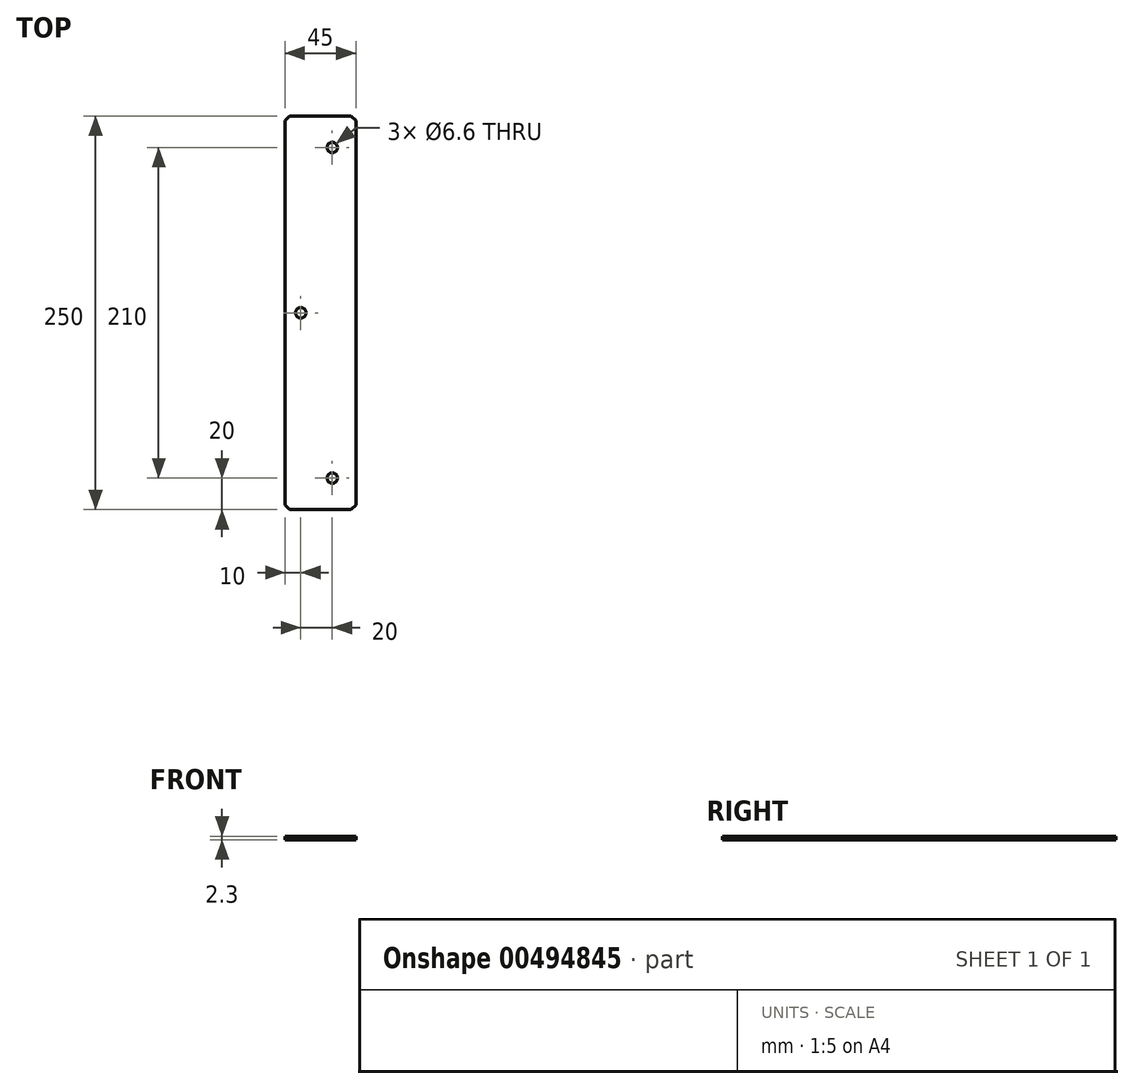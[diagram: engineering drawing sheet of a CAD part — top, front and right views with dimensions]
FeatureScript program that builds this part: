
annotation { "Feature Type Name" : "Feature", "Feature Type Description" : "" }
export const myFeature = defineFeature(function(context is Context, id is Id, definition is map)
    precondition{}
    {
        {
            var Q0;
            Q0=qCreatedBy(makeId("Top.planeOp"),FACE);
            var sketch = newSketch(context, id + "F0", { "sketchPlane" : qUnion([Q0])});
            skLineSegment(sketch, "E0.bottom", {"start": v(0, 0) * mm, "end": v(45, 0) * mm});
            skLineSegment(sketch, "E0.top", {"start": v(0, 250) * mm, "end": v(45, 250) * mm});
            skLineSegment(sketch, "E0.left", {"start": v(0, 0) * mm, "end": v(0, 250) * mm});
            skLineSegment(sketch, "E0.right", {"start": v(45, 0) * mm, "end": v(45, 250) * mm});
            skSolve(sketch);
        }
        {
            var Q0;
            Q0=qSketchRegion(id+"F0",true);
            extrude(context, id + "F1", {"entities" : qUnion([Q0]), "depth" : 2.3 * mm});
        }
        {
            var Q0;
            Q0=makeQuery(id+"F1.opExtrude","CAP_FACE",FACE,{"disambiguationData":[OSD([sQuery(id+"F0.wireOp",EDGE,"E0.bottom"),sQuery(id+"F0.wireOp",EDGE,"E0.top"),sQuery(id+"F0.wireOp",EDGE,"E0.left"),sQuery(id+"F0.wireOp",EDGE,"E0.right")])],"isStart":false});
            var sketch = newSketch(context, id + "F2", { "sketchPlane" : qUnion([Q0])});
            skPoint(sketch, "E1", {"position": v(30, 230) * mm});
            skPoint(sketch, "E2", {"position": v(10, 125) * mm});
            skPoint(sketch, "E3", {"position": v(30, 20) * mm});
            skSolve(sketch);
        }
        {
            var Q0;
            Q0=sQuery(id+"F2.wireOp",VERTEX,"E1");
            var Q1;
            Q1=sQuery(id+"F2.wireOp",VERTEX,"E2");
            var Q2;
            Q2=sQuery(id+"F2.wireOp",VERTEX,"E3");
            var Q3;
            Q3=makeQuery(id+"F1.opExtrude","SWEPT_BODY",BODY,{"disambiguationData":[OSD([sQuery(id+"F0.wireOp",EDGE,"E0.bottom"),sQuery(id+"F0.wireOp",EDGE,"E0.top"),sQuery(id+"F0.wireOp",EDGE,"E0.left"),sQuery(id+"F0.wireOp",EDGE,"E0.right")])]});
            hole(context, id + "F3", {"style" : HoleStyle.SIMPLE, "endStyle" : HoleEndStyle.THROUGH, "standardTappedOrClearance" : lookupTablePath({ "standard" : "ISO", "fit" : "Normal", "size" : "M6", "type" : "Clearance" }), "standardBlindInLast" : lookupTablePath({ "fit" : "Standard", "standard" : "ISO", "size" : "M6", "type" : "Clearance" }), "holeDiameter" : 6.6 * mm, "isTappedThrough" : true, "tappedDepth" : 7.6 * mm, "tapClearance" : 3, "locations" : qUnion([Q0, Q1, Q2]), "scope" : qUnion([Q3])});
        }
        {
            var Q0;
            Q0=makeQuery(id+"F1.opExtrude","SWEPT_EDGE",EDGE,{"disambiguationData":[OSD([sQuery(id+"F0.wireOp",EDGE,"E0.top"),sQuery(id+"F0.wireOp",EDGE,"E0.left")])]});
            var Q1;
            Q1=makeQuery(id+"F1.opExtrude","SWEPT_EDGE",EDGE,{"disambiguationData":[OSD([sQuery(id+"F0.wireOp",EDGE,"E0.top"),sQuery(id+"F0.wireOp",EDGE,"E0.right")])]});
            var Q2;
            Q2=makeQuery(id+"F1.opExtrude","SWEPT_EDGE",EDGE,{"disambiguationData":[OSD([sQuery(id+"F0.wireOp",EDGE,"E0.bottom"),sQuery(id+"F0.wireOp",EDGE,"E0.left")])]});
            var Q3;
            Q3=makeQuery(id+"F1.opExtrude","SWEPT_EDGE",EDGE,{"disambiguationData":[OSD([sQuery(id+"F0.wireOp",EDGE,"E0.bottom"),sQuery(id+"F0.wireOp",EDGE,"E0.right")])]});
            chamfer(context, id + "F4", {"entities" : qUnion([Q0, Q1, Q2, Q3]), "width" : 3 * mm, "tangentPropagation" : true});
        }
    });
